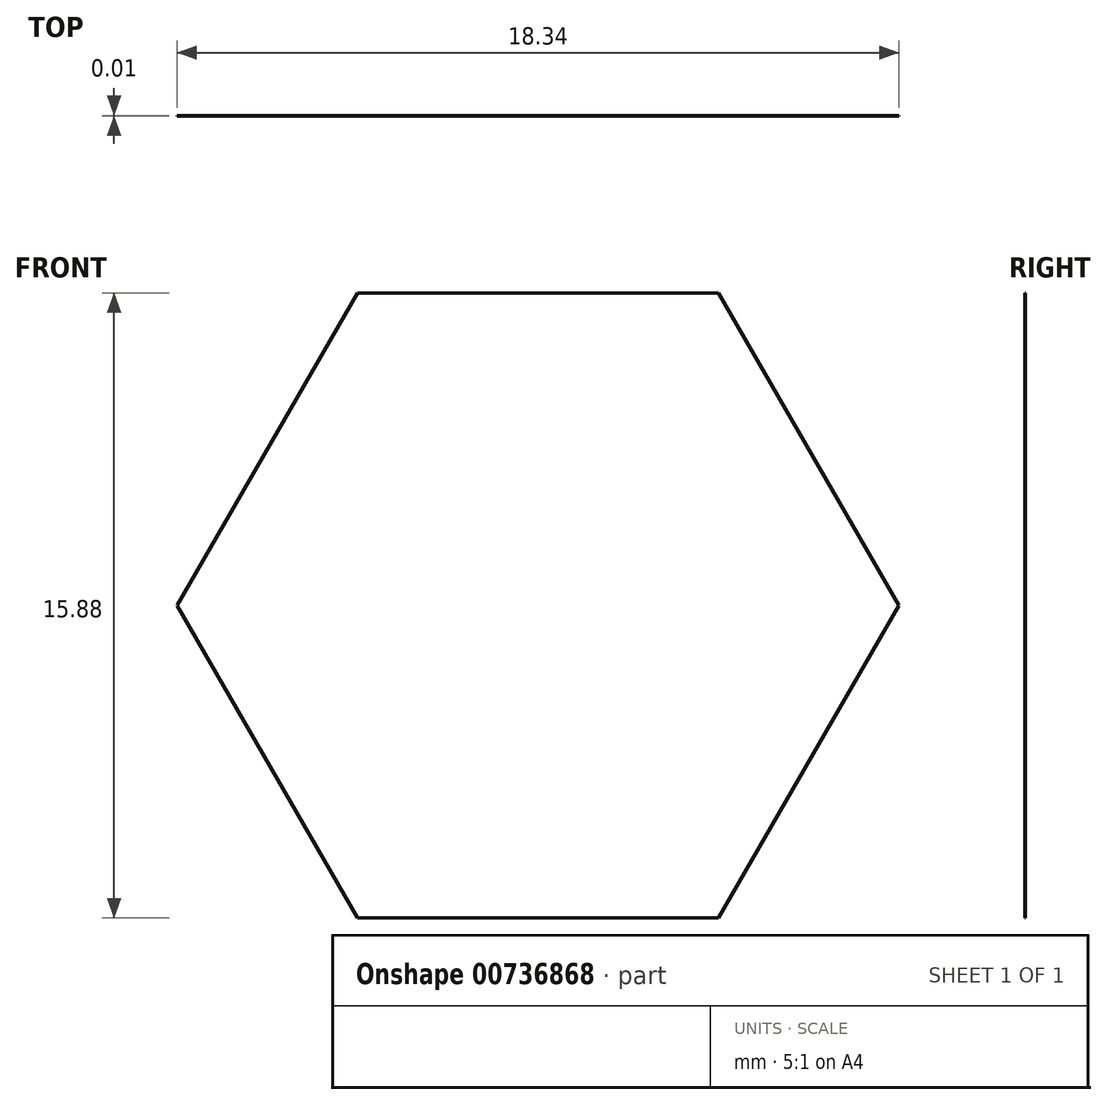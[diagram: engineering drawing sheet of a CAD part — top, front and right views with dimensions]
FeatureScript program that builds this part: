
annotation { "Feature Type Name" : "Feature", "Feature Type Description" : "" }
export const myFeature = defineFeature(function(context is Context, id is Id, definition is map)
    precondition{}
    {
        {
            var Q0;
            Q0=qCreatedBy(makeId("Front.planeOp"),FACE);
            var sketch = newSketch(context, id + "F0", { "sketchPlane" : qUnion([Q0])});
            skCircle(sketch, "E0.cCircle", {"center": v(0, 0) * mm, "radius": 7.94 * mm, "construction": true});
            skLineSegment(sketch, "E0.0", {"start": v(-4.58, 7.94) * mm, "end": v(4.58, 7.94) * mm});
            skLineSegment(sketch, "E0.1", {"start": v(4.58, 7.94) * mm, "end": v(9.17, 0) * mm});
            skLineSegment(sketch, "E0.2", {"start": v(9.17, 0) * mm, "end": v(4.58, -7.94) * mm});
            skLineSegment(sketch, "E0.3", {"start": v(4.58, -7.94) * mm, "end": v(-4.58, -7.94) * mm});
            skLineSegment(sketch, "E0.4", {"start": v(-4.58, -7.94) * mm, "end": v(-9.17, 0) * mm});
            skLineSegment(sketch, "E0.5", {"start": v(-9.17, 0) * mm, "end": v(-4.58, 7.94) * mm});
            skPoint(sketch, "E0.0.midPoint", {"position": v(0, 7.94) * mm});
            skSolve(sketch);
        }
        {
            var Q0;
            Q0 = qSketchRegion(id + "F0", true);
            extrude(context, id + "F1", {"entities" : qUnion([Q0]), "depth" : 9 / 812.8 * mm, "offsetDistance" : 25.4 * mm});
        }
    });
